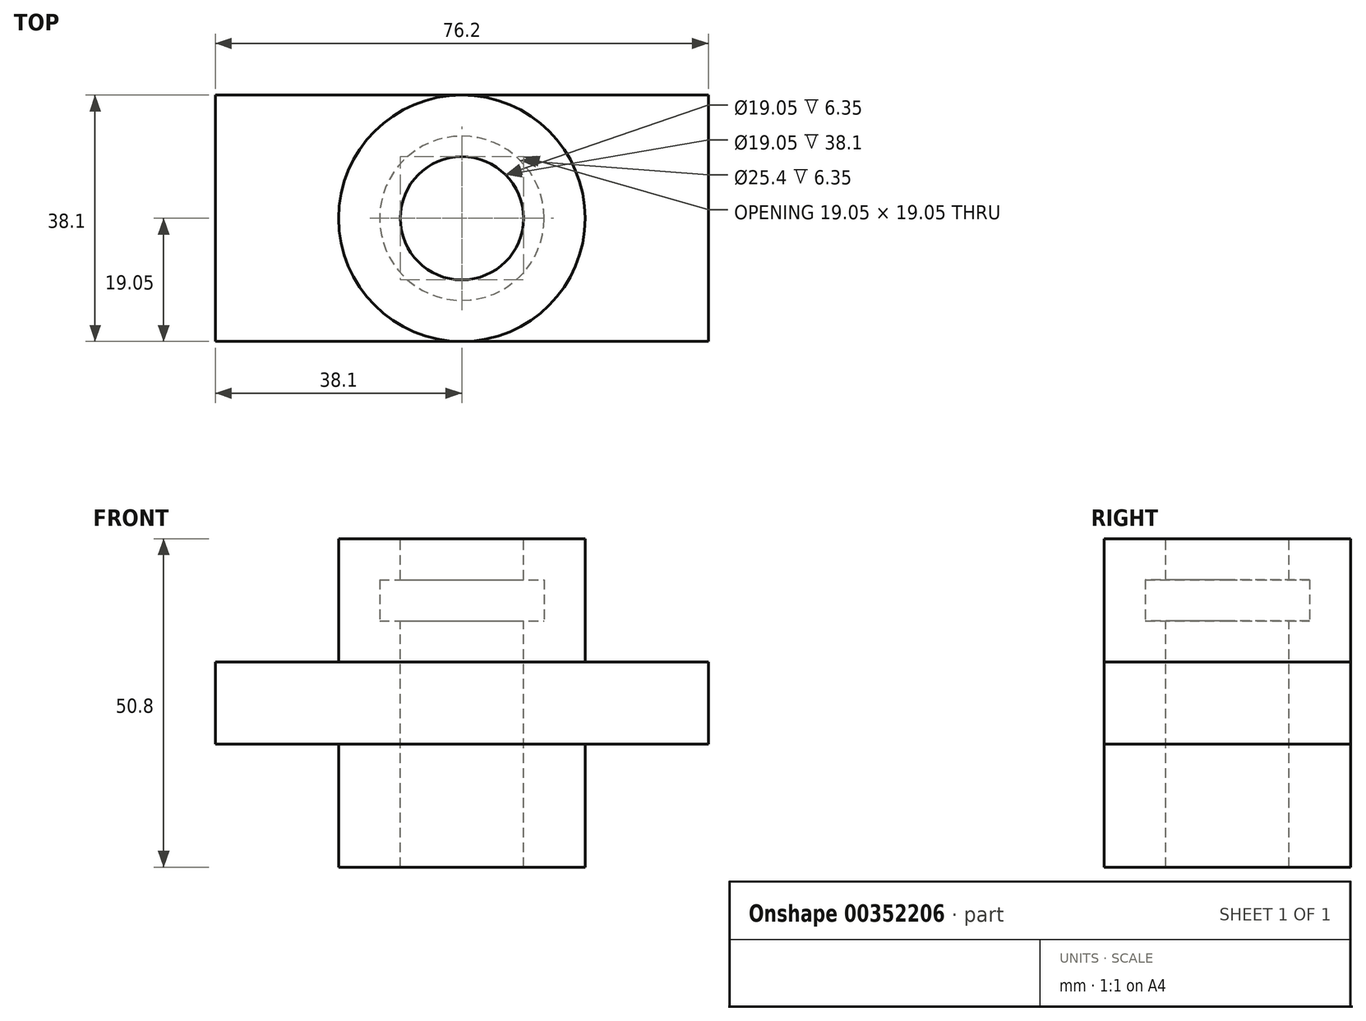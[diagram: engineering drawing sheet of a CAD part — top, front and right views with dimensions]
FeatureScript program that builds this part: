
annotation { "Feature Type Name" : "Feature", "Feature Type Description" : "" }
export const myFeature = defineFeature(function(context is Context, id is Id, definition is map)
    precondition{}
    {
        {
            var Q0;
            Q0=qCreatedBy(makeId("Front.planeOp"),FACE);
            var sketch = newSketch(context, id + "F0", { "sketchPlane" : qUnion([Q0])});
            skLineSegment(sketch, "E0.bottom", {"start": v(-38.1, 12.7) * mm, "end": v(38.1, 12.7) * mm});
            skLineSegment(sketch, "E0.top", {"start": v(-38.1, 0) * mm, "end": v(38.1, 0) * mm});
            skLineSegment(sketch, "E0.left", {"start": v(38.1, 12.7) * mm, "end": v(38.1, 0) * mm});
            skLineSegment(sketch, "E0.right", {"start": v(-38.1, 12.7) * mm, "end": v(-38.1, 0) * mm});
            skSolve(sketch);
        }
        {
            var Q0;
            Q0 = qSketchRegion(id + "F0", true);
            extrude(context, id + "F1", {"entities" : qUnion([Q0]), "endBound" : BoundingType.SYMMETRIC, "depth" : 38.1 * mm});
        }
        {
            var Q0;
            Q0=makeQuery(id+"F1.opExtrude","SWEPT_FACE",FACE,{"disambiguationData":[OSD([sQuery(id+"F0.wireOp",EDGE,"E0.bottom")])]});
            var sketch = newSketch(context, id + "F2", { "sketchPlane" : qUnion([Q0])});
            skCircle(sketch, "E1", {"center": v(0, 0) * mm, "radius": 19.05 * mm});
            skSolve(sketch);
        }
        {
            var Q0;
            Q0 = qSketchRegion(id + "F2", true);
            extrude(context, id + "F3", {"entities" : qUnion([Q0]), "operationType" : NewBodyOperationType.ADD, "depth" : 19.05 * mm, "hasSecondDirection" : true, "secondDirectionOppositeDirection" : true, "secondDirectionDepth" : 31.75 * mm});
        }
        {
            var Q0;
            Q0=makeQuery(id+"F3.opExtrude","CAP_FACE",FACE,{"disambiguationData":[OSD([sQuery(id+"F2.wireOp",EDGE,"E1")])],"isStart":false});
            var sketch = newSketch(context, id + "F4", { "sketchPlane" : qUnion([Q0])});
            skCircle(sketch, "E2", {"center": v(0, 0) * mm, "radius": 9.53 * mm});
            skSolve(sketch);
        }
        {
            var Q0;
            Q0 = qSketchRegion(id + "F4", true);
            extrude(context, id + "F5", {"entities" : qUnion([Q0]), "operationType" : NewBodyOperationType.REMOVE, "endBound" : BoundingType.THROUGH_ALL, "oppositeDirection" : true, "depth" : 25.4 * mm});
        }
        {
            var Q0;
            Q0=qCreatedBy(makeId("Front.planeOp"),FACE);
            var sketch = newSketch(context, id + "F6", { "sketchPlane" : qUnion([Q0])});
            skLineSegment(sketch, "E3", {"start": v(0, 19.05) * mm, "end": v(12.7, 19.05) * mm});
            skLineSegment(sketch, "E4", {"start": v(12.7, 19.05) * mm, "end": v(12.7, 25.4) * mm});
            skPoint(sketch, "E5.orphan", {"position": v(19.05, 31.75) * mm});
            skPoint(sketch, "E6.orphan", {"position": v(-19.05, 31.75) * mm});
            skLineSegment(sketch, "E7", {"start": v(0, 25.4) * mm, "end": v(12.7, 25.4) * mm});
            skLineSegment(sketch, "E8", {"start": v(0, 38.9) * mm, "end": v(0, 0) * mm, "construction": true});
            skPoint(sketch, "E8.startSnap0", {"position": v(0, 25.4) * mm});
            skPoint(sketch, "E8.endSnap0", {"position": v(0, 19.05) * mm});
            skLineSegment(sketch, "E9", {"start": v(0, 25.4) * mm, "end": v(0, 19.05) * mm});
            skSolve(sketch);
        }
        {
            var Q0;
            Q0 = qSketchRegion(id + "F6", true);
            var Q1;
            Q1=sQuery(id+"F6.wireOp",EDGE,"E8");
            revolve(context, id + "F7", {"operationType" : NewBodyOperationType.REMOVE, "entities" : qUnion([Q0]), "axis" : qUnion([Q1]), "revolveType" : RevolveType.FULL, "oppositeDirection" : true});
        }
    });
